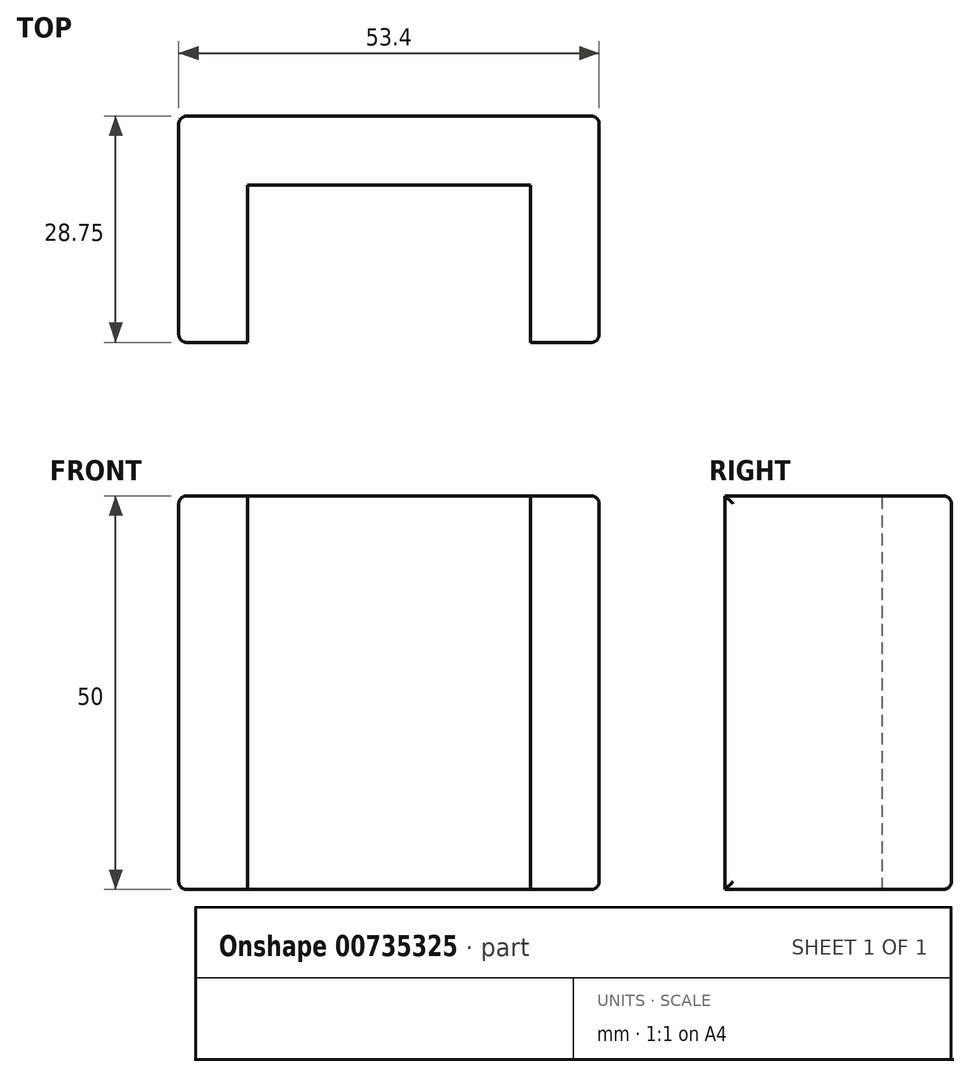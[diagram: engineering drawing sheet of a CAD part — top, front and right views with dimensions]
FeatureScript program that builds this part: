
annotation { "Feature Type Name" : "Feature", "Feature Type Description" : "" }
export const myFeature = defineFeature(function(context is Context, id is Id, definition is map)
    precondition{}
    {
        {
            var Q0;
            Q0=qCreatedBy(makeId("Top.planeOp"),FACE);
            var sketch = newSketch(context, id + "F0", { "sketchPlane" : qUnion([Q0])});
            skLineSegment(sketch, "E0", {"start": v(0, 0) * mm, "end": v(0, 20) * mm});
            skLineSegment(sketch, "E1", {"start": v(0, 20) * mm, "end": v(35.9, 20) * mm});
            skLineSegment(sketch, "E2", {"start": v(35.9, 20) * mm, "end": v(35.9, 0) * mm});
            skLineSegment(sketch, "E3.0", {"start": v(44.65, 28.75) * mm, "end": v(44.65, 0) * mm});
            skLineSegment(sketch, "E3.1", {"start": v(-8.75, 28.75) * mm, "end": v(44.65, 28.75) * mm});
            skLineSegment(sketch, "E3.2", {"start": v(-8.75, 0) * mm, "end": v(-8.75, 28.75) * mm});
            skLineSegment(sketch, "E4", {"start": v(-8.75, 0) * mm, "end": v(0, 0) * mm});
            skLineSegment(sketch, "E5", {"start": v(35.9, 0) * mm, "end": v(44.65, 0) * mm});
            skSolve(sketch);
        }
        {
            var Q0;
            Q0 = qSketchRegion(id + "F0", true);
            extrude(context, id + "F1", {"entities" : qUnion([Q0]), "oppositeDirection" : true, "depth" : 50 * mm, "offsetDistance" : 25 * mm});
        }
        {
            var Q0;
            Q0=makeQuery(id+"F1.opExtrude","SWEPT_FACE",FACE,{"disambiguationData":[OSD([sQuery(id+"F0.wireOp",EDGE,"E3.1")])]});
            var Q1;
            Q1=makeQuery(id+"F1.opExtrude","SWEPT_FACE",FACE,{"disambiguationData":[OSD([sQuery(id+"F0.wireOp",EDGE,"E3.2")])]});
            var Q2;
            Q2=makeQuery(id+"F1.opExtrude","SWEPT_FACE",FACE,{"disambiguationData":[OSD([sQuery(id+"F0.wireOp",EDGE,"E3.0")])]});
            fillet(context, id + "F2", {"entities" : qUnion([Q0, Q1, Q2]), "radius" : 1 * mm, "tangentPropagation" : true, "allowEdgeOverflow" : false});
        }
    });
